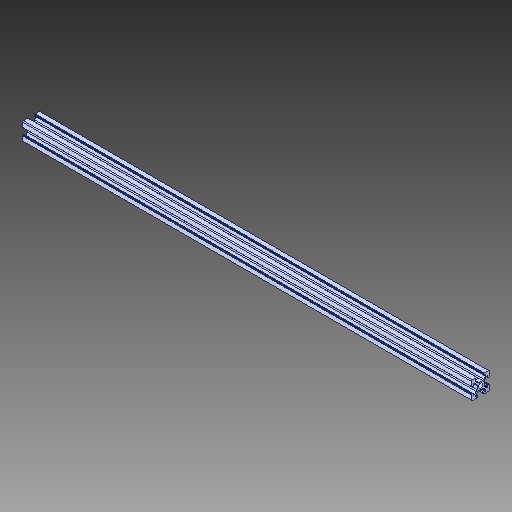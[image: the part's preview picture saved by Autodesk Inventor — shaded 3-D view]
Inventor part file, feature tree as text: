
AUTODESK INVENTOR PART (.ipt)
format: ipt  version: 2018 (Build 220112000, 112)  size: 347,136 bytes
history: native  units: in
note: dims shown in document units (in); Inventor stores cm internally (conversion verified against a paired STEP export)
features: extrude x1, sketch x1, projected_geometry x1, fillet x1
ambient origin geometry x8: Origin, YZ Plane, XZ Plane, XY Plane, X Axis, Y Axis, Z Axis, Center Point
bodies: Solid1 (feature_tree)
feature tree (4):
  extrude  "Extrusion2"  [1 undecoded]
  sketch  "Sketch3"  dims[d2=15.748in d3=0.0in]
  projected_geometry  "Projected Loop2"
  fillet  "Fillet5"  [1 undecoded]
note: 2 required parameter values undecoded (feature->parameter linkage not recoverable at this tier; creation-order binding heuristic only, values carry confidence <= 0.55)
